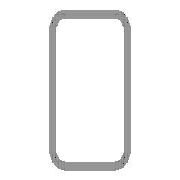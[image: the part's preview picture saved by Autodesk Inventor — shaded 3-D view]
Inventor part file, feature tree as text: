
AUTODESK INVENTOR PART (.ipt)
format: ipt  version: 2025 (Build 290162010, 162A)  size: 134,656 bytes
history: native  units: mm (DEFAULTED — no unit token found)
features: other x4, sketch x1, plane x1
ambient origin geometry x8: Origin, YZ Plane, XZ Plane, XY Plane, X Axis, Y Axis, Z Axis, Center Point
bodies: Solid1 (feature_tree), Body (feature_tree)
feature tree (6):
  parser-record x1  (decoder bookkeeping rows leaked as tree rows — omitted from the tree; the rows remain in map.json)
  other  "Driven Length"
  other  "Start Plane"
  other  "End Plane"
  sketch  "Sketch3"  dims[d3=1090.0mm d4=0.0mm d7=4.0mm d9=40.0mm d11=80.0mm d12=2.0mm d13=80.0mm d14=1170.0mm d15=20.0mm d16=40.0mm d17=90.0deg d18=1090.0mm]
  plane  "Work Plane3"
